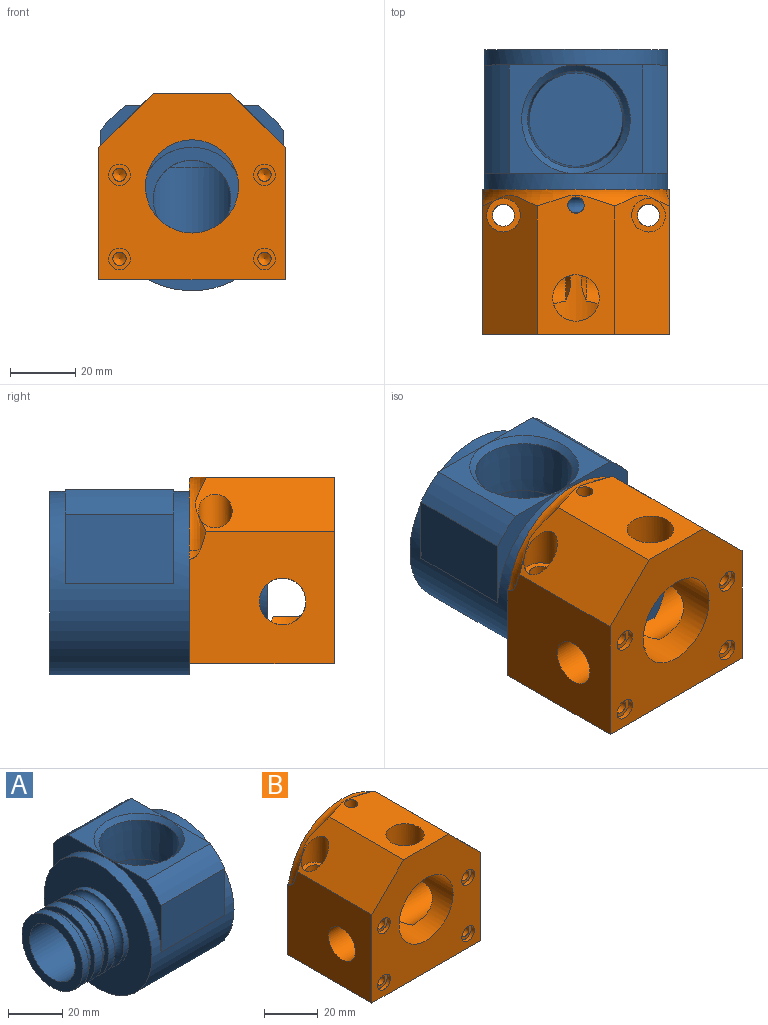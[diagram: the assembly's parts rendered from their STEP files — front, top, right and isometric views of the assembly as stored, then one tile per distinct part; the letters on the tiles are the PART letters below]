
ASSEMBLY  parts=2 mates=1
PART A: 28 faces, bbox 66.7x56.2x56.7 mm
  f0: cylinder r=14.29mm len=28.58mm, axis (0,0,-1), area 1674.9mm2, adj f1,f14,f18
  f1: cylinder r=11.91mm len=37.35mm, axis (1,0,0), area 2591.1mm2, adj f0,f6,f14
  f2: plane 31.75x31.75mm, normal (-1,0,0), area 218.1mm2, adj f5,f11
  f3: cylinder r=15.88mm len=31.75mm, axis (-1,0,0), area 316.7mm2, adj f4,f6
  f4: plane 31.75x31.75mm, normal (1,0,0), area 218.1mm2, adj f3,f5
  f5: cylinder r=13.51mm len=27.03mm, axis (1,0,0), area 269.6mm2, adj f2,f4
  f6: plane 31.75x31.75mm, normal (-1,0,0), area 346.4mm2, adj f1,f3
  f7: cylinder r=15.88mm len=31.75mm, axis (-1,0,0), area 316.7mm2, adj f10,f23
  f8: cylinder r=13.51mm len=27.03mm, axis (1,0,0), area 269.6mm2, adj f9,f10
  f9: plane 31.75x31.75mm, normal (1,0,0), area 218.1mm2, adj f8,f11
  f10: plane 31.75x31.75mm, normal (-1,0,0), area 218.1mm2, adj f7,f8
  f11: cylinder r=15.88mm len=31.75mm, axis (-1,0,0), area 395.9mm2, adj f2,f9
  f12: plane 56.2x56.2mm, normal (-1,0,0), area 1688.7mm2, adj f21,f22
  f13: cone r=14.83mm half-angle=45.9deg, axis (0,0,1), area 252.6mm2, adj f14,f15
  f14: cone r=14.29mm half-angle=1.8deg, axis (0,0,1), area 1577.2mm2, adj f0,f1,f13
  f15: plane 40.85x33.34mm, normal (0,0,1), area 489.8mm2, adj f13,f19,f20,f26,f27
  f16: plane 29.11x0.02mm, normal (0,0,-1), area 0.6mm2, adj f21
  f17: plane 56.2x56.2mm, normal (1,0,0), area 2480.4mm2, adj f21
  f18: plane 28.58x28.58mm, normal (0,0,1), area 641.3mm2, adj f0
  f19: cylinder r=35.12mm len=33.34mm, axis (-1,0,0), area 359.2mm2, adj f15,f24,f26,f27
  f20: cylinder r=35.12mm len=33.34mm, axis (-1,0,0), area 359.2mm2, adj f15,f25,f26,f27
  f21: cylinder r=28.1mm len=56.2mm, axis (-1,0,0), area 4623.9mm2, adj f12,f16,f17,f24,f25,f26,f27
  f22: cylinder r=15.88mm len=31.75mm, axis (-1,0,0), area 237.5mm2, adj f12,f23
  f23: torus R=15.88mm, axis (-1,0,0), area 674.9mm2, adj f7,f22
  f24: plane 33.34x21.07mm, normal (0,-1,0), area 702.6mm2, adj f19,f21,f26,f27
  f25: plane 33.34x21.07mm, normal (0,1,0), area 702.6mm2, adj f20,f21,f26,f27
  f26: plane 56.2x28.58mm, normal (-1,0,0), area 314mm2, adj f15,f19,f20,f21,f24,f25
  f27: plane 56.2x28.58mm, normal (1,0,0), area 314mm2, adj f15,f19,f20,f21,f24,f25
PART B: 43 faces, bbox 75.4x46.6x68.3 mm
  f0: cylinder r=15.88mm len=31.75mm, axis (0,1,0), area 2380.4mm2, adj f1,f2,f11,f12,f13,f14,f15,f17
  f1: cone r=0mm half-angle=59deg, axis (0,1,0), area 9.7mm2, adj f0,f3,f13,f14
  f2: cone r=0mm half-angle=59deg, axis (0,1,0), area 99.6mm2, adj f0,f3,f12,f15
  f3: cylinder r=14.29mm len=28.58mm, axis (0,-1,0), area 1189.8mm2, adj f1,f2,f10,f12,f13,f14,f15,f16
  f4: plane 45.68x41.64mm, normal (-1,0,0), area 1606.1mm2, adj f5,f9,f10,f11,f15,f35,f36
  f5: plane 57.15x44.45mm, normal (0,0,-1), area 2468.6mm2, adj f4,f6,f10,f11,f37,f41
  f6: plane 45.68x41.64mm, normal (1,0,0), area 1606.1mm2, adj f5,f7,f10,f11,f12,f34,f35
  f7: plane 44.84x18.91mm, normal (0.71,0,0.71), area 857mm2, adj f6,f8,f10,f35,f40
  f8: plane 42.68x23.69mm, normal (0,0,1), area 795.5mm2, adj f7,f9,f10,f16,f17,f35
  f9: plane 42.68x16.74mm, normal (-0.71,0,0.71), area 857mm2, adj f4,f8,f10,f35,f39
  f10: plane 57.15x57.15mm, normal (0,-1,0), area 2206.6mm2, adj f3,f4,f5,f6,f7,f8,f9,f20
  f11: plane 57.15x56.9mm, normal (0,1,0), area 2104.5mm2, adj f0,f4,f5,f6,f34,f35,f36
  f12: cylinder r=7.14mm len=25.4mm, axis (1,0,0), area 839.4mm2, adj f0,f2,f3,f6,f13
  f13: cone r=0mm half-angle=59deg, axis (1,0,0), area 19.9mm2, adj f0,f1,f3,f12
  f14: cone r=0mm half-angle=59deg, axis (-1,0,0), area 19.9mm2, adj f0,f1,f3,f15
  f15: cylinder r=7.14mm len=25.4mm, axis (-1,0,0), area 839.5mm2, adj f0,f2,f3,f4,f14
  f16: cylinder r=7.14mm len=16.2mm, axis (0,0,1), area 682.8mm2, adj f3,f8
  f17: cylinder r=2.5mm len=12.9mm, axis (0,0,1), area 200.3mm2, adj f0,f8
  f18: cylinder r=2.02mm len=16.19mm, axis (0,-1,0), area 205.4mm2, adj f19,f21
  f19: plane 6.63x6.63mm, normal (0,-1,0), area 21.7mm2, adj f18,f20
  f20: cylinder r=3.31mm len=6.63mm, axis (0,-1,0), area 33.1mm2, adj f10,f19
  f21: cone r=0mm half-angle=59deg, axis (0,-1,0), area 14.9mm2, adj f18
  f22: cylinder r=2.02mm len=16.19mm, axis (0,-1,0), area 205.4mm2, adj f23,f25
  f23: plane 6.63x6.63mm, normal (0,-1,0), area 21.7mm2, adj f22,f24
  f24: cylinder r=3.31mm len=6.63mm, axis (0,-1,0), area 33.1mm2, adj f10,f23
  f25: cone r=0mm half-angle=59deg, axis (0,-1,0), area 14.9mm2, adj f22
  f26: cylinder r=2.02mm len=16.19mm, axis (0,-1,0), area 205.4mm2, adj f27,f29
  f27: plane 6.63x6.63mm, normal (0,-1,0), area 21.7mm2, adj f26,f28
  f28: cylinder r=3.31mm len=6.63mm, axis (0,-1,0), area 33.1mm2, adj f10,f27
  f29: cone r=0mm half-angle=59deg, axis (0,-1,0), area 14.9mm2, adj f26
  f30: cylinder r=2.02mm len=16.19mm, axis (0,-1,0), area 205.4mm2, adj f31,f33
  f31: plane 6.63x6.63mm, normal (0,-1,0), area 21.7mm2, adj f30,f32
  f32: cylinder r=3.31mm len=6.63mm, axis (0,-1,0), area 33.1mm2, adj f10,f31
  f33: cone r=0mm half-angle=59deg, axis (0,-1,0), area 14.9mm2, adj f30
  f34: torus R=18.8mm, axis (0,-1,0), area 4.9mm2, adj f6,f11,f35
  f35: torus R=34.67mm, axis (0,1,0), area 281mm2, adj f4,f6,f7,f8,f9,f11,f34,f36
  f36: torus R=18.8mm, axis (0,-1,0), area 4.9mm2, adj f4,f11,f35
  f37: cylinder r=3.38mm len=39.37mm, axis (0,0,1), area 835.7mm2, adj f5,f38
  f38: plane 10.31x10.31mm, normal (0,0,1), area 47.7mm2, adj f37,f39
  f39: cylinder r=5.16mm len=12.55mm, axis (0,0,1), area 239.5mm2, adj f9,f38
  f40: cylinder r=5.16mm len=12.55mm, axis (0,0,1), area 239.5mm2, adj f7,f42
  f41: cylinder r=3.38mm len=39.37mm, axis (0,0,1), area 835.7mm2, adj f5,f42
  f42: plane 10.31x10.31mm, normal (0,0,1), area 47.7mm2, adj f40,f41
PLACE A rot(axis=(0,0,1),90deg) t=(0,-23.81,-3.65)mm
PLACE B at identity
MATE revolute A.f20 <-> B.f11  axis (0,-1,0) through (0,0,-3.89)mm
